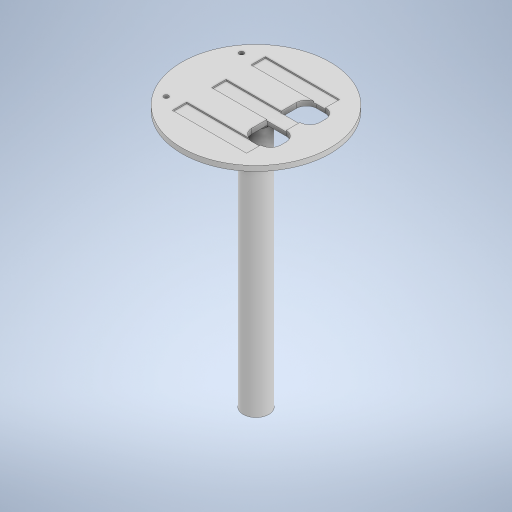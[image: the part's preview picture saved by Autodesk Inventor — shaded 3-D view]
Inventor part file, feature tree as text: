
AUTODESK INVENTOR PART (.ipt)
format: ipt  version: 2024 (Build 280153000, 153)  size: 488,960 bytes
history: native  units: mm
features: extrude x12, sketch x9, projected_geometry x5, fillet x3, other x2, chamfer x1
ambient origin geometry x8: Origin, YZ Plane, XZ Plane, XY Plane, X Axis, Y Axis, Z Axis, Center Point
bodies: Solide1 (feature_tree), Solide2 (feature_tree), Solide3 (feature_tree)
feature tree (32):
  sketch  "Esquisse1"
  extrude  "Extrusion1"  Depth=10.0mm TaperAngle=0.0deg
  extrude  "Extrusion2"  Depth=3.0mm TaperAngle=0.0deg
  sketch  "Esquisse2"
  extrude  "Extrusion3"  Depth=10.95mm
  extrude  "Extrusion4"  TaperAngle=0.0deg  [1 undecoded]
  sketch  "Esquisse3"
  extrude  "Extrusion5"  Depth=43.0mm
  extrude  "Extrusion6"  Depth=1.5mm
  chamfer  "Chanfrein1"  [1 undecoded]
  extrude  "Extrusion7"  Depth=86.7mm
  other  "Plan de construction1"
  sketch  "Esquisse6"
  extrude  "Extrusion8"  Depth=15.0mm
  extrude  "Extrusion9"  Depth=17.0mm
  fillet  "Congé1"  Radius=17.0mm
  fillet  "Congé2"  Radius=10.0mm
  fillet  "Congé3"  Radius=150.0mm
  other  "Scission1"
  extrude  "Extrusion10"  Depth=4.0mm TaperAngle=45.0deg
  extrude  "Extrusion11"  Depth=8.0mm
  extrude  "Extrusion12"  Depth=150.0mm TaperAngle=0.0deg
  projected_geometry  "Boucle projetée1"
  sketch  "Esquisse4"
  sketch  "Esquisse5"
  sketch  "Esquisse8"
  projected_geometry  "Boucle projetée3"
  sketch  "Esquisse9"
  projected_geometry  "Boucle projetée4"
  projected_geometry  "Boucle projetée5"
  projected_geometry  "Boucle projetée6"
  sketch  "Esquisse10"
note: 2 required parameter values undecoded (feature->parameter linkage not recoverable at this tier; creation-order binding heuristic only, values carry confidence <= 0.55)
